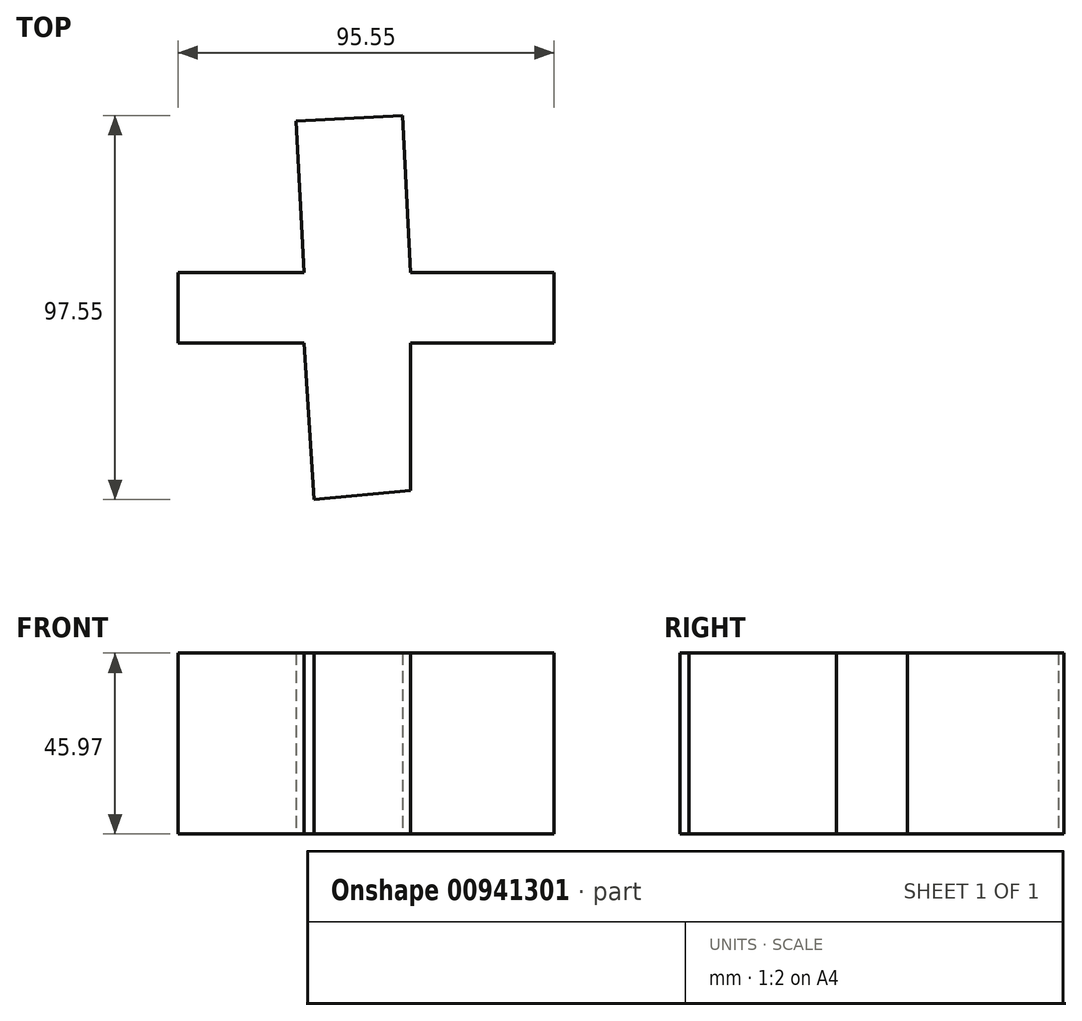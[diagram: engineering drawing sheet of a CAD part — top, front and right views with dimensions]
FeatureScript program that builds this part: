
annotation { "Feature Type Name" : "Feature", "Feature Type Description" : "" }
export const myFeature = defineFeature(function(context is Context, id is Id, definition is map)
    precondition{}
    {
        {
            var Q0;
            Q0=qCreatedBy(makeId("Top.planeOp"),FACE);
            var sketch = newSketch(context, id + "F0", { "sketchPlane" : qUnion([Q0])});
            skLineSegment(sketch, "E0", {"start": v(-16.55, 38.42) * mm, "end": v(-14.53, 0) * mm});
            skLineSegment(sketch, "E1", {"start": v(-16.55, 38.42) * mm, "end": v(10.5, 39.84) * mm});
            skLineSegment(sketch, "E2", {"start": v(10.5, 39.84) * mm, "end": v(12.58, 0) * mm});
            skLineSegment(sketch, "E3", {"start": v(-14.53, 0) * mm, "end": v(-46.48, 0) * mm});
            skLineSegment(sketch, "E4", {"start": v(12.58, 0) * mm, "end": v(49.07, 0) * mm});
            skLineSegment(sketch, "E5", {"start": v(-46.48, 0) * mm, "end": v(-46.48, -17.99) * mm});
            skLineSegment(sketch, "E6", {"start": v(-46.48, -17.99) * mm, "end": v(-14.53, -17.99) * mm});
            skLineSegment(sketch, "E7", {"start": v(49.07, 0) * mm, "end": v(49.07, -17.99) * mm});
            skLineSegment(sketch, "E8", {"start": v(49.07, -17.99) * mm, "end": v(12.58, -17.99) * mm});
            skLineSegment(sketch, "E9", {"start": v(-14.53, -17.99) * mm, "end": v(-11.94, -57.7) * mm});
            skLineSegment(sketch, "E10", {"start": v(12.58, -17.99) * mm, "end": v(12.58, -55.4) * mm});
            skLineSegment(sketch, "E11", {"start": v(-11.94, -57.7) * mm, "end": v(12.58, -55.4) * mm});
            skSolve(sketch);
        }
        {
            var Q0;
            Q0 = qSketchRegion(id + "F0", true);
            extrude(context, id + "F1", {"entities" : qUnion([Q0]), "depth" : 45.97 * mm, "offsetDistance" : 25.4 * mm});
        }
    });
